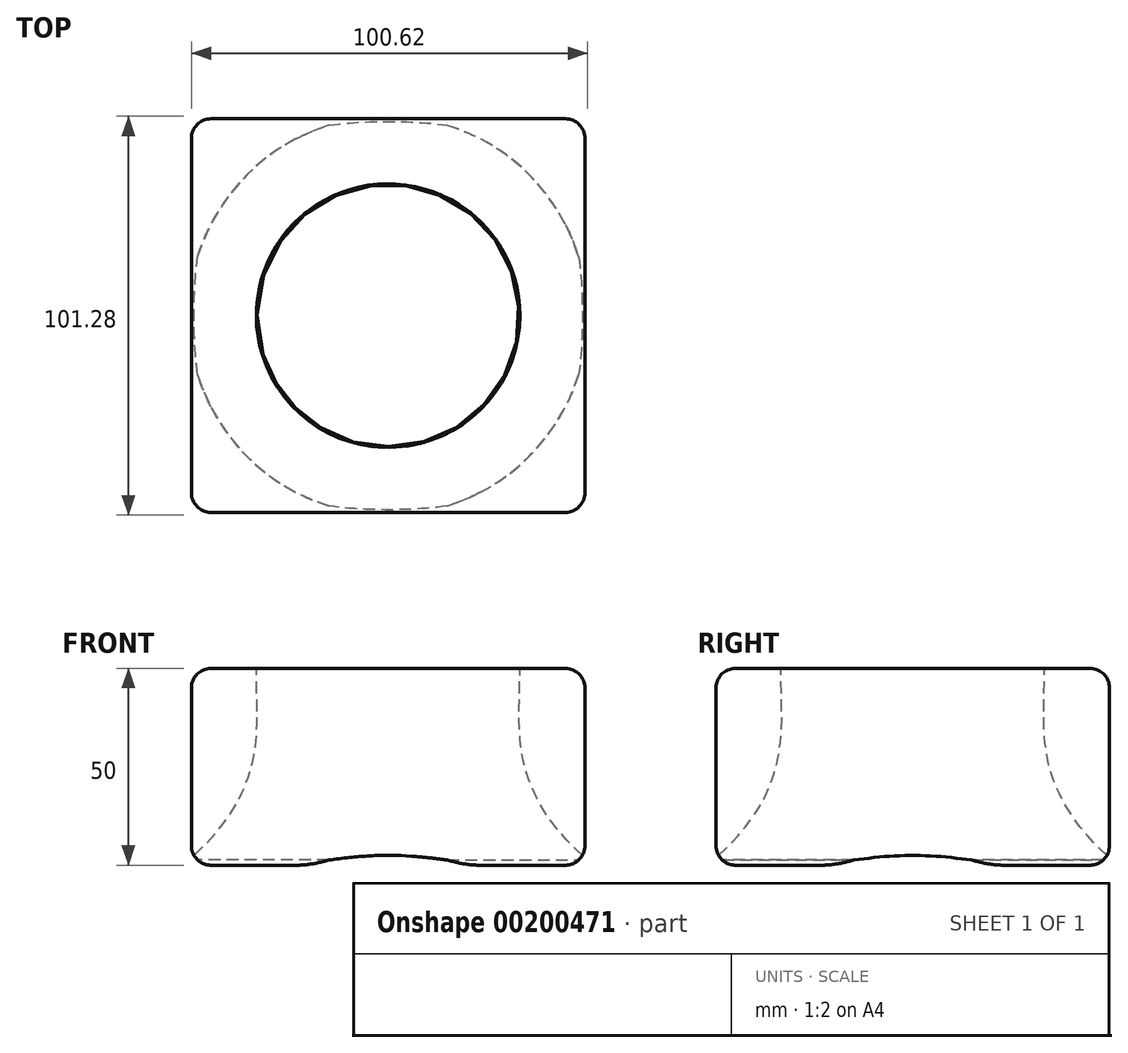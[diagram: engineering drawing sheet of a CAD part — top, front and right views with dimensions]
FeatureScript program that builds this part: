
annotation { "Feature Type Name" : "Feature", "Feature Type Description" : "" }
export const myFeature = defineFeature(function(context is Context, id is Id, definition is map)
    precondition{}
    {
        {
            var Q0;
            Q0=qCreatedBy(makeId("Top.planeOp"),FACE);
            var sketch = newSketch(context, id + "F0", { "sketchPlane" : qUnion([Q0])});
            skLineSegment(sketch, "E0.bottom", {"start": v(-50, 50) * mm, "end": v(50, 50) * mm});
            skLineSegment(sketch, "E0.top", {"start": v(-50, -50) * mm, "end": v(50, -50) * mm});
            skLineSegment(sketch, "E0.left", {"start": v(-50, 50) * mm, "end": v(-50, -50) * mm});
            skLineSegment(sketch, "E0.right", {"start": v(50, 50) * mm, "end": v(50, -50) * mm});
            skPoint(sketch, "E0.middle", {"position": v(0, 0) * mm});
            skSolve(sketch);
        }
        {
            var Q0;
            Q0 = qSketchRegion(id + "F0", true);
            extrude(context, id + "F1", {"entities" : qUnion([Q0]), "depth" : 50 * mm});
        }
        {
            var Q0;
            Q0=qCreatedBy(makeId("Front.planeOp"),FACE);
            var sketch = newSketch(context, id + "F2", { "sketchPlane" : qUnion([Q0])});
            skLineSegment(sketch, "E1", {"start": v(-0.02, -0.47) * mm, "end": v(-0.02, 51.53) * mm});
            skLineSegment(sketch, "E2", {"start": v(-0.02, -0.47) * mm, "end": v(-50.02, -0.47) * mm});
            skLineSegment(sketch, "E3", {"start": v(-0.02, 51.53) * mm, "end": v(-30.02, 51.53) * mm});
            skFitSpline(sketch, "E4.0", {"points": [v(-33.49, 51.5) * mm, v(-33.5, 49.14) * mm, v(-33.4, 44.44) * mm, v(-33.3, 37.53) * mm, v(-33.56, 31.98) * mm, v(-34.17, 27.7) * mm, v(-34.86, 24.58) * mm, v(-35.84, 21.54) * mm, v(-37.52, 17.58) * mm, v(-40.33, 12.75) * mm, v(-44.83, 7.03) * mm, v(-48.59, 3.22) * mm, v(-50.66, 1.3) * mm]});
            skLineSegment(sketch, "E5", {"start": v(-33.49, 51.5) * mm, "end": v(-30.02, 51.53) * mm});
            skLineSegment(sketch, "E6", {"start": v(-50.66, 1.3) * mm, "end": v(-50.66, -0.47) * mm});
            skLineSegment(sketch, "E7", {"start": v(-50.66, -0.47) * mm, "end": v(-50.02, -0.47) * mm});
            skSolve(sketch);
        }
        {
            var Q0;
            Q0 = qSketchRegion(id + "F2", true);
            var Q1;
            Q1=sQuery(id+"F2.wireOp",EDGE,"E1");
            revolve(context, id + "F3", {"operationType" : NewBodyOperationType.REMOVE, "entities" : qUnion([Q0]), "axis" : qUnion([Q1]), "revolveType" : RevolveType.FULL, "oppositeDirection" : true});
        }
        {
            var Q0;
            Q0=makeQuery(id+"F1.opExtrude","CAP_EDGE",EDGE,{"disambiguationData":[OSD([sQuery(id+"F0.wireOp",EDGE,"E0.top")])],"isStart":false});
            var Q1;
            Q1=makeQuery(id+"F1.opExtrude","CAP_EDGE",EDGE,{"disambiguationData":[OSD([sQuery(id+"F0.wireOp",EDGE,"E0.left")])],"isStart":false});
            var Q2;
            Q2=makeQuery(id+"F1.opExtrude","CAP_EDGE",EDGE,{"disambiguationData":[OSD([sQuery(id+"F0.wireOp",EDGE,"E0.bottom")])],"isStart":false});
            var Q3;
            Q3=makeQuery(id+"F1.opExtrude","CAP_EDGE",EDGE,{"disambiguationData":[OSD([sQuery(id+"F0.wireOp",EDGE,"E0.right")])],"isStart":false});
            var Q4;
            {var subQ0=sQuery(id+"F0.wireOp",EDGE,"E0.right");var subQ1=sQuery(id+"F0.wireOp",EDGE,"E0.top");Q4=makeQuery(id+"F3.boolean.opBoolean","SPLIT",EDGE,{"disambiguationData":[TD([makeQuery(id+"F1.opExtrude","SWEPT_FACE",FACE,{"disambiguationData":[OSD([subQ0])]})])],"derivedFrom":makeQuery(id+"F1.opExtrude","CAP_EDGE",EDGE,{"disambiguationData":[OSD([subQ1])],"isStart":true})});}
            var Q5;
            {var subQ0=sQuery(id+"F0.wireOp",EDGE,"E0.left");var subQ1=sQuery(id+"F0.wireOp",EDGE,"E0.top");Q5=makeQuery(id+"F3.boolean.opBoolean","SPLIT",EDGE,{"disambiguationData":[TD([makeQuery(id+"F1.opExtrude","SWEPT_FACE",FACE,{"disambiguationData":[OSD([subQ0])]})])],"derivedFrom":makeQuery(id+"F1.opExtrude","CAP_EDGE",EDGE,{"disambiguationData":[OSD([subQ1])],"isStart":true})});}
            var Q6;
            {var subQ0=sQuery(id+"F0.wireOp",EDGE,"E0.right");var subQ1=sQuery(id+"F0.wireOp",EDGE,"E0.top");Q6=makeQuery(id+"F3.boolean.opBoolean","SPLIT",EDGE,{"disambiguationData":[TD([makeQuery(id+"F1.opExtrude","SWEPT_FACE",FACE,{"disambiguationData":[OSD([subQ1])]})])],"derivedFrom":makeQuery(id+"F1.opExtrude","CAP_EDGE",EDGE,{"disambiguationData":[OSD([subQ0])],"isStart":true})});}
            var Q7;
            {var subQ0=sQuery(id+"F0.wireOp",EDGE,"E0.bottom");var subQ1=sQuery(id+"F0.wireOp",EDGE,"E0.right");Q7=makeQuery(id+"F3.boolean.opBoolean","SPLIT",EDGE,{"disambiguationData":[TD([makeQuery(id+"F1.opExtrude","SWEPT_FACE",FACE,{"disambiguationData":[OSD([subQ0])]})])],"derivedFrom":makeQuery(id+"F1.opExtrude","CAP_EDGE",EDGE,{"disambiguationData":[OSD([subQ1])],"isStart":true})});}
            var Q8;
            {var subQ0=sQuery(id+"F0.wireOp",EDGE,"E0.bottom");var subQ1=sQuery(id+"F0.wireOp",EDGE,"E0.right");Q8=makeQuery(id+"F3.boolean.opBoolean","SPLIT",EDGE,{"disambiguationData":[TD([makeQuery(id+"F1.opExtrude","SWEPT_FACE",FACE,{"disambiguationData":[OSD([subQ1])]})])],"derivedFrom":makeQuery(id+"F1.opExtrude","CAP_EDGE",EDGE,{"disambiguationData":[OSD([subQ0])],"isStart":true})});}
            var Q9;
            {var subQ0=sQuery(id+"F0.wireOp",EDGE,"E0.bottom");var subQ1=sQuery(id+"F0.wireOp",EDGE,"E0.left");Q9=makeQuery(id+"F3.boolean.opBoolean","SPLIT",EDGE,{"disambiguationData":[TD([makeQuery(id+"F1.opExtrude","SWEPT_FACE",FACE,{"disambiguationData":[OSD([subQ1])]})])],"derivedFrom":makeQuery(id+"F1.opExtrude","CAP_EDGE",EDGE,{"disambiguationData":[OSD([subQ0])],"isStart":true})});}
            var Q10;
            {var subQ0=sQuery(id+"F0.wireOp",EDGE,"E0.bottom");var subQ1=sQuery(id+"F0.wireOp",EDGE,"E0.left");Q10=makeQuery(id+"F3.boolean.opBoolean","SPLIT",EDGE,{"disambiguationData":[TD([makeQuery(id+"F1.opExtrude","SWEPT_FACE",FACE,{"disambiguationData":[OSD([subQ0])]})])],"derivedFrom":makeQuery(id+"F1.opExtrude","CAP_EDGE",EDGE,{"disambiguationData":[OSD([subQ1])],"isStart":true})});}
            var Q11;
            {var subQ0=sQuery(id+"F0.wireOp",EDGE,"E0.left");var subQ1=sQuery(id+"F0.wireOp",EDGE,"E0.top");Q11=makeQuery(id+"F3.boolean.opBoolean","SPLIT",EDGE,{"disambiguationData":[TD([makeQuery(id+"F1.opExtrude","SWEPT_FACE",FACE,{"disambiguationData":[OSD([subQ1])]})])],"derivedFrom":makeQuery(id+"F1.opExtrude","CAP_EDGE",EDGE,{"disambiguationData":[OSD([subQ0])],"isStart":true})});}
            var Q12;
            Q12=makeQuery(id+"F1.opExtrude","SWEPT_EDGE",EDGE,{"disambiguationData":[OSD([sQuery(id+"F0.wireOp",EDGE,"E0.top"),sQuery(id+"F0.wireOp",EDGE,"E0.right")])]});
            var Q13;
            Q13=makeQuery(id+"F1.opExtrude","SWEPT_EDGE",EDGE,{"disambiguationData":[OSD([sQuery(id+"F0.wireOp",EDGE,"E0.bottom"),sQuery(id+"F0.wireOp",EDGE,"E0.left")])]});
            var Q14;
            Q14=makeQuery(id+"F1.opExtrude","SWEPT_EDGE",EDGE,{"disambiguationData":[OSD([sQuery(id+"F0.wireOp",EDGE,"E0.bottom"),sQuery(id+"F0.wireOp",EDGE,"E0.right")])]});
            var Q15;
            Q15=makeQuery(id+"F1.opExtrude","SWEPT_EDGE",EDGE,{"disambiguationData":[OSD([sQuery(id+"F0.wireOp",EDGE,"E0.top"),sQuery(id+"F0.wireOp",EDGE,"E0.left")])]});
            fillet(context, id + "F4", {"entities" : qUnion([Q0, Q1, Q2, Q3, Q4, Q5, Q6, Q7, Q8, Q9, Q10, Q11, Q12, Q13, Q14, Q15]), "radius" : 5 * mm, "tangentPropagation" : true, "allowEdgeOverflow" : false});
        }
    });
